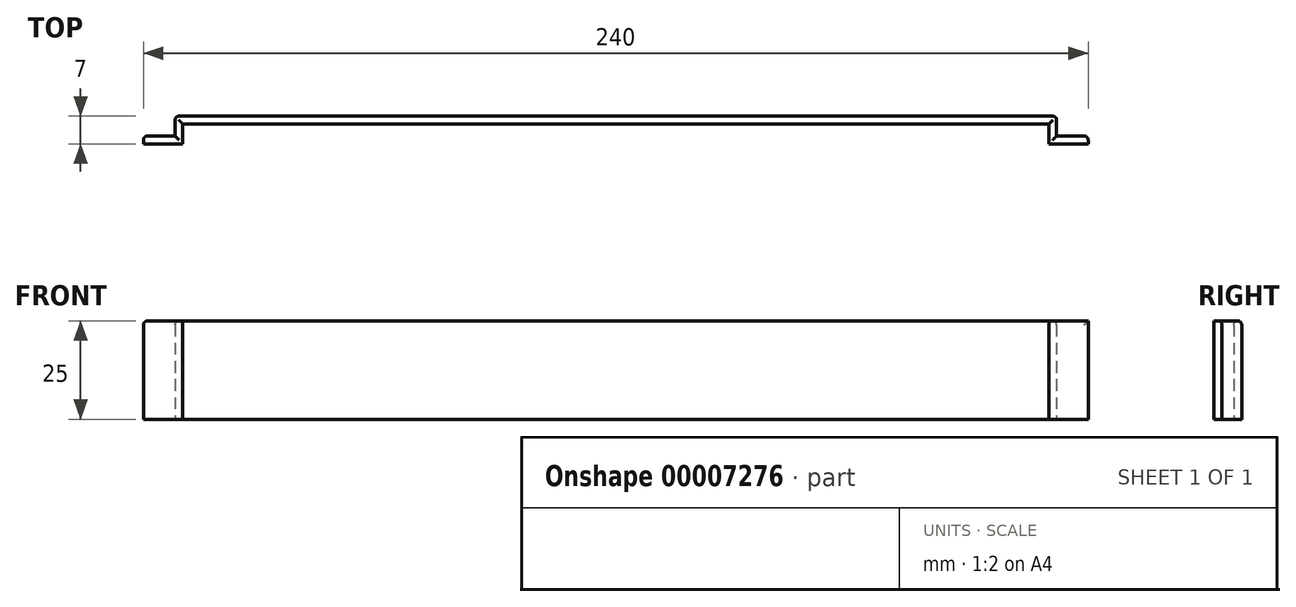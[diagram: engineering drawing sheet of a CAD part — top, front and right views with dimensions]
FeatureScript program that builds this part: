
annotation { "Feature Type Name" : "Feature", "Feature Type Description" : "" }
export const myFeature = defineFeature(function(context is Context, id is Id, definition is map)
    precondition{}
    {
        {
            var Q0;
            Q0=qCreatedBy(makeId("Top.planeOp"),FACE);
            var sketch = newSketch(context, id + "F0", { "sketchPlane" : qUnion([Q0])});
            skLineSegment(sketch, "E0", {"start": v(0, 0) * mm, "end": v(-110, 0) * mm});
            skLineSegment(sketch, "E1", {"start": v(-110, 0) * mm, "end": v(-110, -5) * mm});
            skLineSegment(sketch, "E2", {"start": v(-110, -5) * mm, "end": v(-120, -5) * mm});
            skLineSegment(sketch, "E3", {"start": v(-120, -5) * mm, "end": v(-120, -3) * mm});
            skLineSegment(sketch, "E4", {"start": v(-120, -3) * mm, "end": v(-112, -3) * mm});
            skLineSegment(sketch, "E5", {"start": v(-112, -3) * mm, "end": v(-112, 2) * mm});
            skLineSegment(sketch, "E6", {"start": v(-112, 2) * mm, "end": v(0, 2) * mm});
            skLineSegment(sketch, "E7", {"start": v(0, 0) * mm, "end": v(0, 11.63) * mm, "construction": true});
            skLineSegment(sketch, "E8.0.MirrorCS", {"start": v(120, -5) * mm, "end": v(120, -3) * mm});
            skLineSegment(sketch, "E8.1.MirrorCS", {"start": v(0, 0) * mm, "end": v(110, 0) * mm});
            skLineSegment(sketch, "E8.2.MirrorCS", {"start": v(112, -3) * mm, "end": v(112, 2) * mm});
            skLineSegment(sketch, "E8.3.MirrorCS", {"start": v(112, 2) * mm, "end": v(0, 2) * mm});
            skLineSegment(sketch, "E8.4.MirrorCS", {"start": v(120, -3) * mm, "end": v(112, -3) * mm});
            skLineSegment(sketch, "E8.5.MirrorCS", {"start": v(110, 0) * mm, "end": v(110, -5) * mm});
            skLineSegment(sketch, "E8.6.MirrorCS", {"start": v(110, -5) * mm, "end": v(120, -5) * mm});
            skSolve(sketch);
        }
        {
            var Q0;
            Q0 = qSketchRegion(id + "F0", true);
            extrude(context, id + "F1", {"entities" : qUnion([Q0]), "depth" : 25 * mm});
        }
        {
            var Q0;
            Q0=makeQuery(id+"F1.opExtrude","CAP_EDGE",EDGE,{"disambiguationData":[OSD([sQuery(id+"F0.wireOp",EDGE,"E0"),sQuery(id+"F0.wireOp",EDGE,"E8.1.MirrorCS")])],"isStart":false});
            var Q1;
            Q1=makeQuery(id+"F1.opExtrude","CAP_EDGE",EDGE,{"disambiguationData":[OSD([sQuery(id+"F0.wireOp",EDGE,"E6"),sQuery(id+"F0.wireOp",EDGE,"E8.3.MirrorCS")])],"isStart":false});
            fillet(context, id + "F2", {"entities" : qUnion([Q0, Q1]), "radius" : 1 * mm, "tangentPropagation" : true, "allowEdgeOverflow" : false});
        }
        {
            var Q0;
            Q0=makeQuery(id+"F1.opExtrude","CAP_EDGE",EDGE,{"disambiguationData":[OSD([sQuery(id+"F0.wireOp",EDGE,"E1")])],"isStart":false});
            var Q1;
            Q1=makeQuery(id+"F1.opExtrude","CAP_EDGE",EDGE,{"disambiguationData":[OSD([sQuery(id+"F0.wireOp",EDGE,"E5")])],"isStart":false});
            var Q2;
            Q2=makeQuery(id+"F1.opExtrude","CAP_EDGE",EDGE,{"disambiguationData":[OSD([sQuery(id+"F0.wireOp",EDGE,"E4")])],"isStart":false});
            var Q3;
            Q3=makeQuery(id+"F1.opExtrude","CAP_EDGE",EDGE,{"disambiguationData":[OSD([sQuery(id+"F0.wireOp",EDGE,"E8.5.MirrorCS")])],"isStart":false});
            var Q4;
            Q4=makeQuery(id+"F1.opExtrude","CAP_EDGE",EDGE,{"disambiguationData":[OSD([sQuery(id+"F0.wireOp",EDGE,"E8.2.MirrorCS")])],"isStart":false});
            var Q5;
            Q5=makeQuery(id+"F1.opExtrude","CAP_EDGE",EDGE,{"disambiguationData":[OSD([sQuery(id+"F0.wireOp",EDGE,"E8.4.MirrorCS")])],"isStart":false});
            var Q6;
            Q6=makeQuery(id+"F1.opExtrude","SWEPT_EDGE",EDGE,{"disambiguationData":[OSD([sQuery(id+"F0.wireOp",EDGE,"E8.0.MirrorCS"),sQuery(id+"F0.wireOp",EDGE,"E8.4.MirrorCS")])]});
            fillet(context, id + "F3", {"entities" : qUnion([Q0, Q1, Q2, Q3, Q4, Q5, Q6]), "radius" : 1 * mm, "tangentPropagation" : true, "allowEdgeOverflow" : false});
        }
        {
            var Q0;
            Q0=makeQuery(id+"F1.opExtrude","SWEPT_EDGE",EDGE,{"disambiguationData":[OSD([sQuery(id+"F0.wireOp",EDGE,"E3"),sQuery(id+"F0.wireOp",EDGE,"E4")])]});
            fillet(context, id + "F4", {"entities" : qUnion([Q0]), "radius" : 1 * mm, "tangentPropagation" : true, "allowEdgeOverflow" : false});
        }
    });
